# Revit family: EIHLS-L-280-1240x
name_source: partatom
category: Leuchten
units: mm (PartAtom-declared; Revit-internal decimal feet)

## family parameters
Basisbauteil = Fläche
Beim Laden mit Abzugskörper schneiden = Nein
Bemaßung runder Anschluss = Durchmesser verwenden
Gemeinsam genutzt = Nein
Lichtquelle = Ja
OmniClass-Nummer = 23.80.70.11
OmniClass-Titel = Luminaries for Internal Lighting
Raumberechnungspunkt = Nein
Teiletyp = Normal

## types (4) — shared parameters
Baugruppenkennzeichen = D5020200
Emissionsform beim Rendern sichtbar = Nein
Farbfilter = 16777215
Farbtemperaturverschiebung bei Dämpfen der Lampe = <Keine Auswahl>
Hersteller = RIDI Leuchten GmbH
Lampe = LED
Neigungswinkel = 90.00°
Scheinlast = 96 VA
URL = www.ridi.de
Von Breite des Rechtecks ausssenden = 1496 mm  [stored 4.90814 ft]
Von Länge des Rechtecks aussenden = 256 mm  [stored 0.839895 ft]
brand = RIDI
conformity mark = CE
electrical safety class = 1
height = 81 mm  [stored 0.265748 ft]
ingress protection (IP) code = IP64
length = 1548 mm  [stored 5.07874 ft]
nominal frequency = 50-60Hz
nominal voltage = 230
rated input power = 96
voltage type (AC, DC, UC) = AC
width = 312 mm  [stored 1.02362 ft]
zero-valued in all types: Vorgabe-Ansicht

## per-type parameters (varying)
| type | Datei für fotometrisches Netz | Modell | weight |
| EIHLS-L 280/1240-840 SM | EIHLS-L 2801240-840 SM.IES | 0850585 | 15.0 kg |
| EIHLS-L 280/1240-840 SB | EIHLS-L 2801240-840 SB.IES | 0850457 | 12.6 kg |
| EIHLS-L 280/1240-840 OS | EIHLS-L 2801240-840 OS.IES | 0850467 | 12.6 kg |
| EIHLS-L 280/1240-840 SM-DA | EIHLS-L 2801240-840 SM.IES | 0860585 | 15.0 kg |

note: column(s) folded — value = type name in every type: product name

note: [stored X ft] marks values corroborated as IEEE doubles in the binary element streams (Revit-internal decimal feet)
